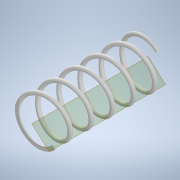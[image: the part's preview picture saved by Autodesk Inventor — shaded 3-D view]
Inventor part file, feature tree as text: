
AUTODESK INVENTOR PART (.ipt)
format: ipt  version: 2021 (Build 250183000, 183)  size: 445,952 bytes
history: native  units: mm
features: other x3, sketch x3, sweep x1, extrude x1
ambient origin geometry x8: Origin, YZ Plane, XZ Plane, XY Plane, X Axis, Y Axis, Z Axis, Center Point
bodies: Body1 (feature_tree)
feature tree (8):
  other  "Bryła1"
  sketch  "Szkic 3D1"
  other  "Płaszczyzna konstrukcyjna1"
  sweep  "Przeciągnięcie1"
  extrude  "Wyciągnięcie proste1"  TaperAngle=0.0deg  [1 undecoded]
  other  "Krzywa śrubowa1"
  sketch  "Szkic1"
  sketch  "Szkic2"
note: 1 required parameter value undecoded (feature->parameter linkage not recoverable at this tier; creation-order binding heuristic only, values carry confidence <= 0.55)
